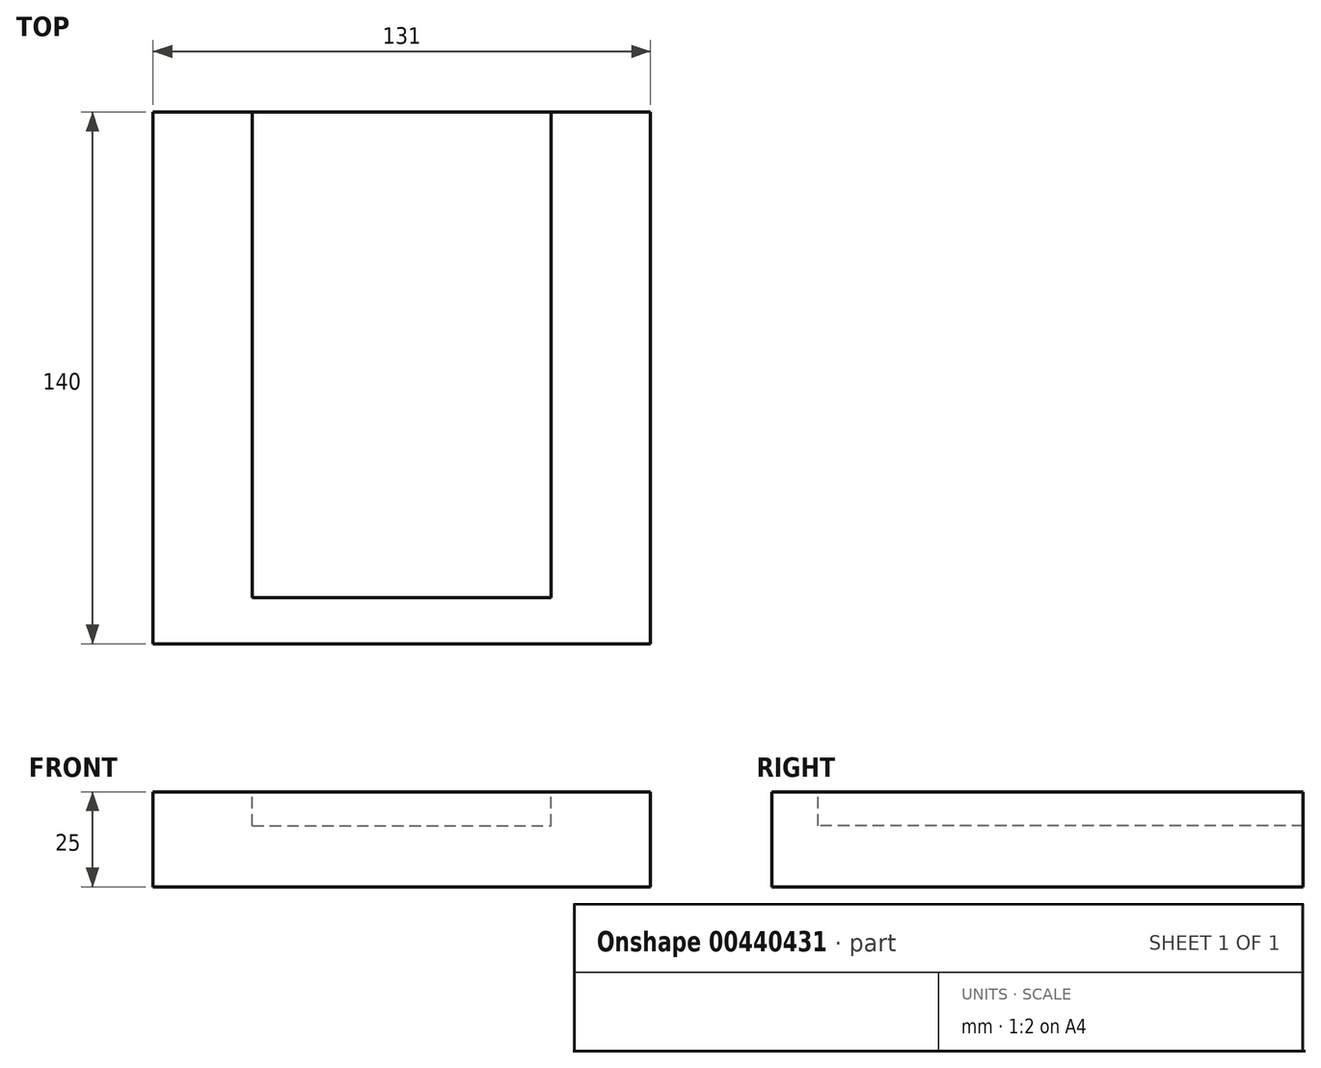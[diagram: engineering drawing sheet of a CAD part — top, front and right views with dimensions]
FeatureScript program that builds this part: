
annotation { "Feature Type Name" : "Feature", "Feature Type Description" : "" }
export const myFeature = defineFeature(function(context is Context, id is Id, definition is map)
    precondition{}
    {
        {
            var Q0;
            Q0=qCreatedBy(makeId("Top.planeOp"),FACE);
            var sketch = newSketch(context, id + "F0", { "sketchPlane" : qUnion([Q0])});
            skLineSegment(sketch, "E0", {"start": v(-65.5, 0) * mm, "end": v(-65.5, 70) * mm});
            skLineSegment(sketch, "E1", {"start": v(0, 70) * mm, "end": v(-65.5, 70) * mm});
            skLineSegment(sketch, "E2", {"start": v(-65.5, 0) * mm, "end": v(-65.5, -70) * mm});
            skLineSegment(sketch, "E3", {"start": v(0, -70) * mm, "end": v(-65.5, -70) * mm});
            skLineSegment(sketch, "E4", {"start": v(0, 70) * mm, "end": v(65.5, 70) * mm});
            skLineSegment(sketch, "E5", {"start": v(65.5, 0) * mm, "end": v(65.5, 70) * mm});
            skLineSegment(sketch, "E6", {"start": v(0, -70) * mm, "end": v(65.5, -70) * mm});
            skLineSegment(sketch, "E7", {"start": v(65.5, 0) * mm, "end": v(65.5, -69.56) * mm});
            skLineSegment(sketch, "E8", {"start": v(65.5, -69.56) * mm, "end": v(65.5, -70) * mm});
            skSolve(sketch);
        }
        {
            var Q0;
            Q0=makeQuery(id+"F0.imprint","IMPRINT",FACE,{"disambiguationData":[TD([[makeQuery(id+"F0.imprint","IMPRINT",EDGE,{"derivedFrom":sQuery(id+"F0.wireOp",EDGE,"E0")}),-1.0]])]});
            extrude(context, id + "F1", {"entities" : qUnion([Q0]), "depth" : 15 * mm});
        }
        {
            var Q0;
            Q0=makeQuery(id+"F1.opExtrude","CAP_FACE",FACE,{"disambiguationData":[OSD([sQuery(id+"F0.wireOp",EDGE,"E0"),sQuery(id+"F0.wireOp",EDGE,"E1"),sQuery(id+"F0.wireOp",EDGE,"E2"),sQuery(id+"F0.wireOp",EDGE,"E3"),sQuery(id+"F0.wireOp",EDGE,"E4"),sQuery(id+"F0.wireOp",EDGE,"E5"),sQuery(id+"F0.wireOp",EDGE,"E6"),sQuery(id+"F0.wireOp",EDGE,"E7"),sQuery(id+"F0.wireOp",EDGE,"E8")])],"isStart":false});
            extrude(context, id + "F2", {"entities" : qUnion([Q0]), "operationType" : NewBodyOperationType.ADD, "depth" : 10 * mm});
        }
        {
            var Q0;
            Q0=makeQuery(id+"F2.opExtrude","CAP_FACE",FACE,{"disambiguationData":[OSD([sQuery(id+"F0.wireOp",EDGE,"E0"),sQuery(id+"F0.wireOp",EDGE,"E1"),sQuery(id+"F0.wireOp",EDGE,"E2"),sQuery(id+"F0.wireOp",EDGE,"E3"),sQuery(id+"F0.wireOp",EDGE,"E4"),sQuery(id+"F0.wireOp",EDGE,"E5"),sQuery(id+"F0.wireOp",EDGE,"E6"),sQuery(id+"F0.wireOp",EDGE,"E7"),sQuery(id+"F0.wireOp",EDGE,"E8")])],"isStart":false});
            var sketch = newSketch(context, id + "F3", { "sketchPlane" : qUnion([Q0])});
            skPoint(sketch, "E9.endSnap0", {"position": v(0, 70) * mm});
            skLineSegment(sketch, "E10", {"start": v(0, 70) * mm, "end": v(-39.37, 70) * mm});
            skLineSegment(sketch, "E11.MirrorCS", {"start": v(0, 70) * mm, "end": v(39.37, 70) * mm});
            skLineSegment(sketch, "E12", {"start": v(-39.37, 70) * mm, "end": v(-39.37, -57.92) * mm});
            skLineSegment(sketch, "E13", {"start": v(39.37, 70) * mm, "end": v(39.37, -57.85) * mm});
            skLineSegment(sketch, "E14", {"start": v(0, -57.85) * mm, "end": v(-39.37, -57.85) * mm});
            skLineSegment(sketch, "E15", {"start": v(0, -57.85) * mm, "end": v(39.37, -57.85) * mm});
            skSolve(sketch);
        }
        {
            var Q0;
            {var subQ1=sQuery(id+"F3.wireOp",EDGE,"E10");Q0=makeQuery(id+"F3.imprint","IMPRINT",FACE,{"disambiguationData":[TD([[makeQuery(id+"F3.imprint","IMPRINT",EDGE,{"derivedFrom":subQ1}),-1.0]])]});}
            extrude(context, id + "F4", {"entities" : qUnion([Q0]), "operationType" : NewBodyOperationType.REMOVE, "oppositeDirection" : true, "depth" : 8.9 * mm});
        }
    });
